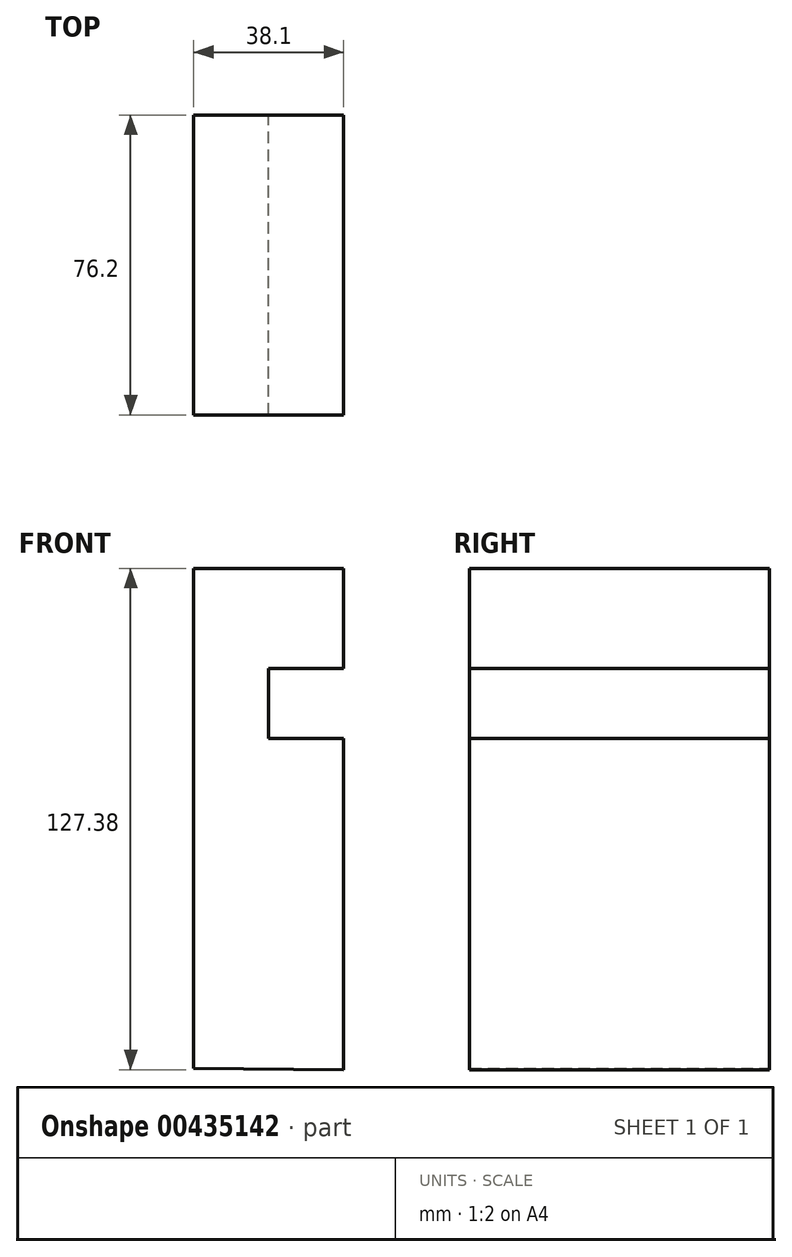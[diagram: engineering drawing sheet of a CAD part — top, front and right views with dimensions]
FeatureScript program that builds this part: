
annotation { "Feature Type Name" : "Feature", "Feature Type Description" : "" }
export const myFeature = defineFeature(function(context is Context, id is Id, definition is map)
    precondition{}
    {
        {
            var Q0;
            Q0=qCreatedBy(makeId("Front.planeOp"),FACE);
            var sketch = newSketch(context, id + "F0", { "sketchPlane" : qUnion([Q0])});
            skLineSegment(sketch, "E0", {"start": v(0, -56.52) * mm, "end": v(0, 70.48) * mm});
            skLineSegment(sketch, "E1", {"start": v(0, 70.48) * mm, "end": v(38.1, 70.48) * mm});
            skLineSegment(sketch, "E2", {"start": v(38.1, 70.48) * mm, "end": v(38.1, 45.08) * mm});
            skLineSegment(sketch, "E3", {"start": v(38.1, 45.08) * mm, "end": v(19.05, 45.08) * mm});
            skLineSegment(sketch, "E4", {"start": v(19.05, 45.08) * mm, "end": v(19.05, 27.3) * mm});
            skLineSegment(sketch, "E5", {"start": v(19.05, 27.3) * mm, "end": v(38.1, 27.3) * mm});
            skLineSegment(sketch, "E6", {"start": v(38.1, 27.3) * mm, "end": v(38.1, -56.9) * mm});
            skLineSegment(sketch, "E7", {"start": v(38.1, -56.9) * mm, "end": v(0, -56.52) * mm});
            skSolve(sketch);
        }
        {
            var Q0;
            Q0=makeQuery(id+"F0.imprint","IMPRINT",FACE,{"disambiguationData":[TD([[makeQuery(id+"F0.imprint","IMPRINT",EDGE,{"derivedFrom":sQuery(id+"F0.wireOp",EDGE,"E0")}),-1.0]])]});
            extrude(context, id + "F1", {"entities" : qUnion([Q0]), "depth" : 76.2 * mm});
        }
    });
